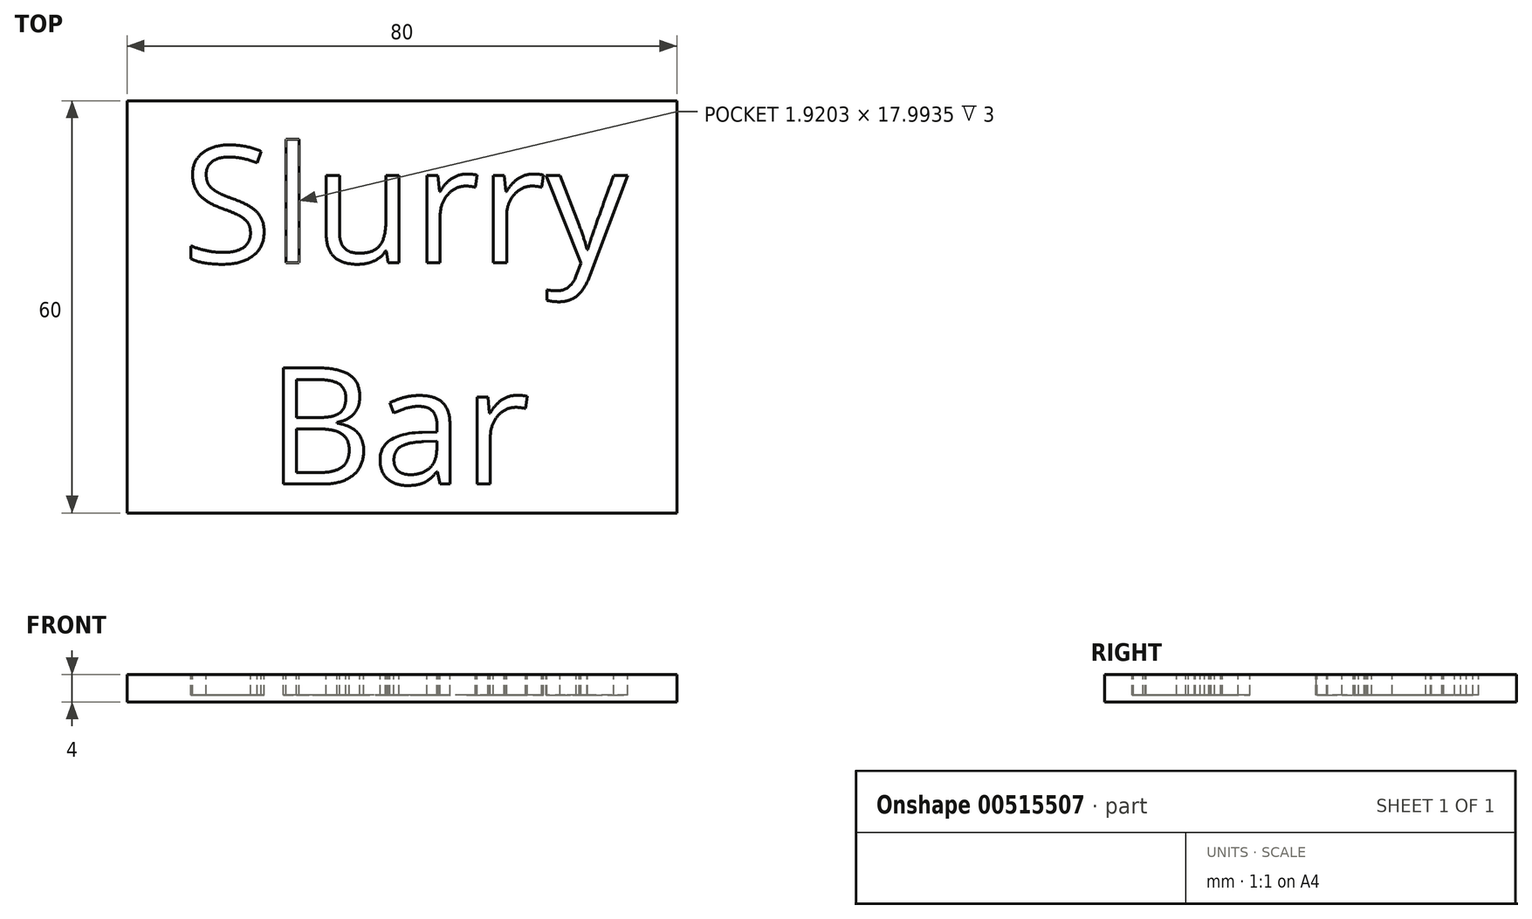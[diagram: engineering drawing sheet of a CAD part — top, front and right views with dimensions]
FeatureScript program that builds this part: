
annotation { "Feature Type Name" : "Feature", "Feature Type Description" : "" }
export const myFeature = defineFeature(function(context is Context, id is Id, definition is map)
    precondition{}
    {
        {
            var Q0;
            Q0=qCreatedBy(makeId("Top.planeOp"),FACE);
            var sketch = newSketch(context, id + "F0", { "sketchPlane" : qUnion([Q0])});
            skLineSegment(sketch, "E0.bottom", {"start": v(-41.25, 21.65) * mm, "end": v(38.75, 21.65) * mm});
            skLineSegment(sketch, "E0.top", {"start": v(-41.25, -38.35) * mm, "end": v(38.75, -38.35) * mm});
            skLineSegment(sketch, "E0.left", {"start": v(-41.25, 21.65) * mm, "end": v(-41.25, -38.35) * mm});
            skLineSegment(sketch, "E0.right", {"start": v(38.75, 21.65) * mm, "end": v(38.75, -38.35) * mm});
            skSolve(sketch);
        }
        {
            var Q0;
            Q0=makeQuery(id+"F0.imprint","IMPRINT",FACE,{"disambiguationData":[TD([[makeQuery(id+"F0.imprint","IMPRINT",EDGE,{"derivedFrom":sQuery(id+"F0.wireOp",EDGE,"E0.bottom")}),-1.0]])]});
            extrude(context, id + "F1", {"entities" : qUnion([Q0]), "oppositeDirection" : true, "depth" : 4 * mm, "offsetDistance" : 25 * mm});
        }
        {
            var Q0;
            Q0=qCreatedBy(makeId("Top.planeOp"),FACE);
            var sketch = newSketch(context, id + "F2", { "sketchPlane" : qUnion([Q0])});
            skText(sketch, "E1", { "text": "Slurry\n  Bar ", "fontName": "OpenSans-Regular.ttf"});
            const initialGuessF2  = {"E1": [-0.03316, -0.00191, 1, 0, 0.01705]};
            skSetInitialGuess(sketch, initialGuessF2);
            skSolve(sketch);
        }
        {
            var Q0;
            Q0 = qSketchRegion(id + "F2", true);
            extrude(context, id + "F3", {"entities" : qUnion([Q0]), "operationType" : NewBodyOperationType.REMOVE, "oppositeDirection" : true, "depth" : 3 * mm, "offsetDistance" : 25 * mm});
        }
    });
